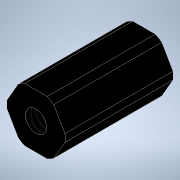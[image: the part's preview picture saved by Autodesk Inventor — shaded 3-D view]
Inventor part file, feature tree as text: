
AUTODESK INVENTOR PART (.ipt)
format: ipt  version: 2022.3 (Build 263350000, 350)  size: 113,152 bytes
history: native  units: in
note: dims shown in document units (in); Inventor stores cm internally (conversion verified against a paired STEP export)
features: sketch x2, extrude x1, hole x1
ambient origin geometry x8: Origin, YZ Plane, XZ Plane, XY Plane, X Axis, Y Axis, Z Axis, Center Point
bodies: Solid1 (feature_tree)
feature tree (4):
  extrude  "Extrusion1"  Depth=0.5in
  hole  "Hole1"  [1 undecoded]
  sketch  "Sketch1"  dims[d0=0.5in d1=0.5413in]
  sketch  "Sketch2"  dims[d2=1.0in d3=0.0in d4=0.196in d5=0.5in d6=0.507in d7=0.25in d8=0.5635in d9=1.0in d10=0.8108in]
note: 1 required parameter value undecoded (feature->parameter linkage not recoverable at this tier; creation-order binding heuristic only, values carry confidence <= 0.55)
